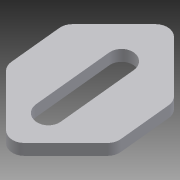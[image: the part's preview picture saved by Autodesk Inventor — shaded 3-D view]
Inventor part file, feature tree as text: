
AUTODESK INVENTOR PART (.ipt)
format: ipt  version: 2014 (Build 180170000, 170)  size: 114,688 bytes
history: native  units: in
note: dims shown in document units (in); Inventor stores cm internally (conversion verified against a paired STEP export)
features: extrude x2, sketch x2, fillet x1
ambient origin geometry x8: Origin, YZ Plane, XZ Plane, XY Plane, X Axis, Y Axis, Z Axis, Center Point
bodies: Solid1 (feature_tree)
feature tree (5):
  extrude  "Extrusion1"  Depth=0.285in
  extrude  "Extrusion7"  Depth=0.0625in
  fillet  "Fillet13"  Radius=0.18in
  sketch  "Sketch2"  dims[d1=0.375in d2=0.285in]
  sketch  "Sketch3"  dims[d3=0.0625in d4=0.0in d5=0.355in d6=0.18in d31=0.12in d39=0.375in d40=0.375in d41=0.0in d42=0.0in d43=0.0625in]
